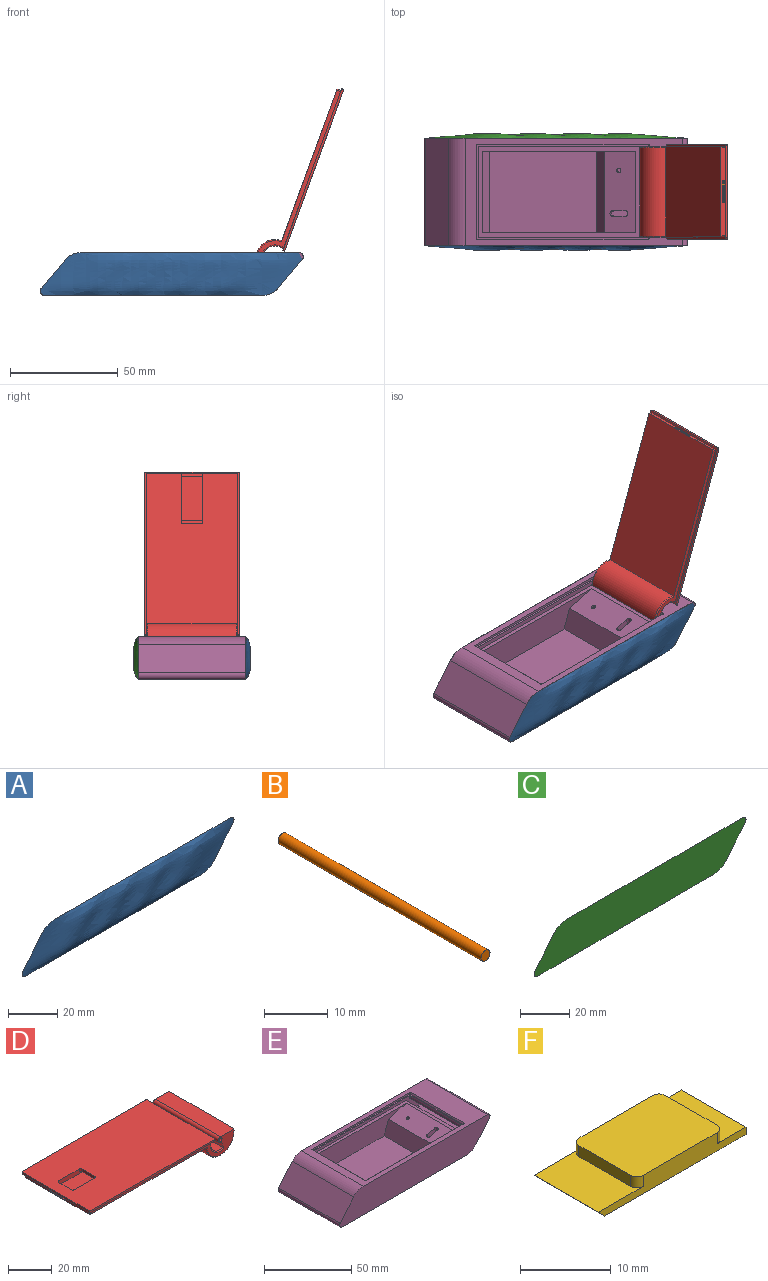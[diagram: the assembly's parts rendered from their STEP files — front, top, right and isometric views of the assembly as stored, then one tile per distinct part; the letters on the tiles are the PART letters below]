
ASSEMBLY  parts=6 mates=5
PART A: 2 faces, bbox 122.5x3.4x21.2 mm
  f0: plane 122.43x20.21mm, normal (0,1,0), area 2185.9mm2, adj f1
  f1: bspline ~122.31x20.97mm, area 2254.9mm2, adj f0
PART B: 3 faces, bbox 2x45x2 mm
  f0: cylinder r=1mm len=45mm, axis (0,1,0), area 282.7mm2, adj f1,f2
  f1: plane 2x2mm, normal (0,-1,0), area 3.1mm2, adj f0
  f2: plane 2x2mm, normal (0,1,0), area 3.1mm2, adj f0
PART C: 2 faces, bbox 122.5x3.4x21.2 mm
  f0: plane 122.43x20.21mm, normal (0,-1,0), area 2185.9mm2, adj f1
  f1: bspline ~122.31x20.97mm, area 2254.9mm2, adj f0
PART D: 38 faces, bbox 94.7x44x13.2 mm
  f0: plane 80.53x44mm, normal (0,0,1), area 3393.8mm2, adj f13,f14,f15,f16,f17,f18,f19,f20
  f1: plane 10x6mm, normal (0,0,-1), area 50.4mm2, adj f3,f30,f31,f35,f36,f37
  f2: cylinder r=6mm len=41mm, axis (0,1,0), area 555.9mm2, adj f8,f12,f22,f25
  f3: plane 41x2mm, normal (-1,0,0), area 72mm2, adj f1,f4,f12,f21,f24,f28,f30,f31
  f4: plane 75.5x42mm, normal (0,0,-1), area 3150mm2, adj f3,f5,f10,f11,f21,f23,f24,f26
  f5: cylinder r=9mm len=41mm, axis (0,1,0), area 1221mm2, adj f4,f6,f23,f26
  f6: plane 42x8.87mm, normal (0,0,1), area 372.6mm2, adj f5,f7,f10,f11,f23,f26
  f7: cylinder r=1.5mm len=42mm, axis (0,1,0), area 219.9mm2, adj f6,f8,f10,f11
  f8: plane 42x4.7mm, normal (-0.94,0,-0.34), area 189.1mm2, adj f2,f7,f10,f11,f22,f25
  f9: cylinder r=1mm len=42mm, axis (0,1,0), area 263.9mm2, adj f10,f11
  f10: plane 92x10.5mm, normal (0,-1,0), area 240.6mm2, adj f4,f6,f7,f8,f9,f12,f24,f25
  f11: plane 92x10.5mm, normal (0,1,0), area 240.6mm2, adj f4,f6,f7,f8,f9,f12,f21,f22
  f12: plane 80x44mm, normal (0,0,-1), area 229.6mm2, adj f2,f3,f10,f11,f13,f14,f15,f16
  f13: plane 43x1mm, normal (-1,0,0), area 43mm2, adj f0,f12,f17,f19
  f14: cylinder r=5.39mm len=43mm, axis (0,1,0), area 48.7mm2, adj f0,f12,f18,f20
  f15: plane 79.44x1mm, normal (0,-1,0), area 79.2mm2, adj f0,f12,f19,f20
  f16: plane 79.44x1mm, normal (0,1,0), area 79.2mm2, adj f0,f12,f17,f18
  f17: cylinder r=0.5mm len=1mm, axis (0,0,-1), area 0.8mm2, adj f0,f12,f13,f16
  f18: torus R=5.89mm, axis (0,-1,0), area 0.9mm2, adj f0,f12,f14,f16
  f19: cylinder r=0.5mm len=1mm, axis (0,0,1), area 0.8mm2, adj f0,f12,f13,f15
  f20: torus R=5.89mm, axis (0,-1,0), area 0.9mm2, adj f0,f12,f14,f15
  f21: cylinder r=0.5mm len=2mm, axis (0,0,-1), area 1.6mm2, adj f3,f4,f11,f12
  f22: torus R=6.5mm, axis (0,-1,0), area 10.9mm2, adj f2,f8,f11,f12
  f23: torus R=8.5mm, axis (0,-1,0), area 22.9mm2, adj f4,f5,f6,f11
  f24: cylinder r=0.5mm len=2mm, axis (0,0,1), area 1.6mm2, adj f3,f4,f10,f12
  f25: torus R=6.5mm, axis (0,-1,0), area 10.9mm2, adj f2,f8,f10,f12
  f26: torus R=8.5mm, axis (0,-1,0), area 22.9mm2, adj f4,f5,f6,f10
  f27: plane 10x6mm, normal (0,0,-1), area 50.4mm2, adj f29,f30,f31,f32,f33,f34
  f28: plane 25x10mm, normal (0,0,1), area 250mm2, adj f3,f29,f30,f31
  f29: plane 10x1mm, normal (-1,0,0), area 10mm2, adj f27,f28,f30,f31
  f30: plane 25x2.5mm, normal (0,1,0), area 44.5mm2, adj f0,f1,f3,f27,f28,f29,f32,f37
  f31: plane 25x2.5mm, normal (0,-1,0), area 44.5mm2, adj f0,f1,f3,f27,f28,f29,f34,f35
  f32: cylinder r=1mm len=1.5mm, axis (0,0,1), area 2.4mm2, adj f0,f27,f30,f33
  f33: plane 8x1.5mm, normal (-1,0,0), area 12mm2, adj f0,f27,f32,f34
  f34: cylinder r=1mm len=1.5mm, axis (0,0,1), area 2.4mm2, adj f0,f27,f31,f33
  f35: cylinder r=1mm len=1.5mm, axis (0,0,1), area 2.4mm2, adj f0,f1,f31,f36
  f36: plane 8x1.5mm, normal (1,0,0), area 12mm2, adj f0,f1,f35,f37
  f37: cylinder r=1mm len=1.5mm, axis (0,0,1), area 2.4mm2, adj f0,f1,f30,f36
PART E: 95 faces, bbox 122.2x50x20.5 mm
  f0: plane 38x14.46mm, normal (-0.27,0,0.96), area 545.9mm2, adj f1,f36,f37,f38,f43,f44,f45,f46
  f1: plane 75.5x42mm, normal (0,0,1), area 452mm2, adj f0,f17,f19,f20,f25,f27,f30,f33
  f2: plane 101.05x50mm, normal (0,0,1), area 1509.4mm2, adj f3,f9,f10,f11,f12,f14,f15,f16
  f3: cylinder r=10mm len=50mm, axis (0,1,0), area 436.3mm2, adj f2,f4,f10,f11
  f4: plane 50x13.14mm, normal (-0.77,0,0.64), area 857.8mm2, adj f3,f5,f10,f11
  f5: cylinder r=2mm len=50mm, axis (0,1,0), area 226.9mm2, adj f4,f6,f10,f11
  f6: plane 101.05x50mm, normal (0,0,-1), area 5052.4mm2, adj f5,f7,f10,f11
  f7: cylinder r=10mm len=50mm, axis (0,1,0), area 436.3mm2, adj f6,f8,f10,f11
  f8: plane 50x13.14mm, normal (0.77,0,-0.64), area 857.8mm2, adj f7,f9,f10,f11
  f9: cylinder r=2mm len=50mm, axis (0,1,0), area 226.9mm2, adj f2,f8,f10,f11
  f10: plane 122.2x20mm, normal (0,-1,0), area 2185.9mm2, adj f2,f3,f4,f5,f6,f7,f8,f9
  f11: plane 122.2x20mm, normal (0,1,0), area 2185.9mm2, adj f2,f3,f4,f5,f6,f7,f8,f9
  f12: plane 43x1mm, normal (1,0,0), area 43mm2, adj f2,f13,f21,f23
  f13: plane 80x44mm, normal (0,0,1), area 229.6mm2, adj f12,f14,f15,f16,f17,f18,f19,f20
  f14: cylinder r=5.39mm len=43mm, axis (0,1,0), area 48.7mm2, adj f2,f13,f22,f24
  f15: plane 79.44x1mm, normal (0,1,0), area 79.2mm2, adj f2,f13,f23,f24
  f16: plane 79.44x1mm, normal (0,-1,0), area 79.2mm2, adj f2,f13,f21,f22
  f17: plane 41x2mm, normal (1,0,0), area 72mm2, adj f1,f13,f25,f27,f59,f60,f61,f62
  f18: cylinder r=6mm len=41mm, axis (0,-1,0), area 83.6mm2, adj f13,f26,f28,f29
  f19: plane 92x10.5mm, normal (0,-1,0), area 279mm2, adj f1,f13,f27,f28,f29,f31,f32,f57
  f20: plane 92x10.5mm, normal (0,1,0), area 279mm2, adj f1,f13,f25,f26,f29,f31,f32,f56
  f21: cylinder r=0.5mm len=1mm, axis (0,0,1), area 0.8mm2, adj f2,f12,f13,f16
  f22: torus R=5.89mm, axis (0,-1,0), area 0.9mm2, adj f2,f13,f14,f16
  f23: cylinder r=0.5mm len=1mm, axis (0,0,-1), area 0.8mm2, adj f2,f12,f13,f15
  f24: torus R=5.89mm, axis (0,-1,0), area 0.9mm2, adj f2,f13,f14,f15
  f25: cylinder r=0.5mm len=2mm, axis (0,0,1), area 1.6mm2, adj f1,f13,f17,f20
  f26: torus R=6.5mm, axis (0,-1,0), area 1.6mm2, adj f13,f18,f20,f29
  f27: cylinder r=0.5mm len=2mm, axis (0,0,-1), area 1.6mm2, adj f1,f13,f17,f19
  f28: torus R=6.5mm, axis (0,-1,0), area 1.6mm2, adj f13,f18,f19,f29
  f29: plane 42x5mm, normal (0,0,-1), area 189.1mm2, adj f18,f19,f20,f26,f28,f32
  f30: cylinder r=9mm len=41mm, axis (0,1,0), area 1221mm2, adj f1,f31,f63,f64
  f31: plane 42x8.87mm, normal (0,0,-1), area 372.6mm2, adj f19,f20,f30,f32,f63,f64
  f32: cylinder r=1.5mm len=42mm, axis (0,1,0), area 99mm2, adj f19,f20,f29,f31
  f33: plane 38x4mm, normal (0.8,0,0.6), area 190mm2, adj f1,f34,f37,f38
  f34: plane 38x10mm, normal (1,0,0), area 380mm2, adj f33,f35,f37,f38
  f35: plane 50x38mm, normal (0,0,1), area 1900mm2, adj f34,f36,f37,f38
  f36: plane 38x10mm, normal (-0.94,0,0.33), area 403.1mm2, adj f0,f35,f37,f38
  f37: plane 71x14mm, normal (0,-1,0), area 766.8mm2, adj f0,f1,f33,f34,f35,f36
  f38: plane 71x14mm, normal (0,1,0), area 766.8mm2, adj f0,f1,f33,f34,f35,f36
  f39: plane 3x1.93mm, normal (-0.96,0,-0.27), area 6mm2, adj f40,f42,f47,f54
  f40: plane 3.42x2.73mm, normal (0,-1,0), area 6mm2, adj f39,f41,f47,f54
  f41: plane 3x1.93mm, normal (0.96,0,0.27), area 6mm2, adj f40,f42,f47,f54
  f42: plane 3.42x2.73mm, normal (0,1,0), area 6mm2, adj f39,f41,f47,f54
  f43: plane 6.58x4.49mm, normal (0,1,0), area 18mm2, adj f0,f44,f46,f47
  f44: cylinder r=1.3mm len=3.24mm, axis (-0.27,0,0.96), area 12.3mm2, adj f0,f43,f45,f47
  f45: plane 6.58x4.49mm, normal (0,-1,0), area 18mm2, adj f0,f44,f46,f47
  f46: cylinder r=1.3mm len=3.24mm, axis (-0.27,0,0.96), area 12.3mm2, adj f0,f43,f45,f47
  f47: plane 42x12.15mm, normal (0.27,0,-0.96), area 499.6mm2, adj f39,f40,f41,f42,f43,f44,f45,f46
  f48: plane 42x17.2mm, normal (0,0,1), area 722.3mm2, adj f49,f50,f51,f52
  f49: plane 42x9.89mm, normal (-0.96,0,-0.27), area 430.9mm2, adj f47,f48,f51,f52
  f50: plane 42x6.53mm, normal (0.94,0,-0.33), area 290.8mm2, adj f47,f48,f51,f52
  f51: plane 17.2x9.89mm, normal (0,1,0), area 120.8mm2, adj f47,f48,f49,f50
  f52: plane 17.2x9.89mm, normal (0,-1,0), area 120.8mm2, adj f47,f48,f49,f50
  f53: cylinder r=1mm len=2.19mm, axis (-0.27,0,0.96), area 6.3mm2, adj f0,f54
  f54: plane 3x2.89mm, normal (0.27,0,-0.96), area 5.9mm2, adj f39,f40,f41,f42,f53
  f55: plane 2x2mm, normal (0,1,0), area 3.1mm2, adj f56
  f56: cylinder r=1mm len=2mm, axis (0,1,0), area 9.4mm2, adj f20,f55
  f57: cylinder r=1mm len=2mm, axis (0,1,0), area 9.4mm2, adj f19,f58
  f58: plane 2x2mm, normal (0,-1,0), area 3.1mm2, adj f57
  f59: plane 10x1mm, normal (0,0,-1), area 10mm2, adj f17,f60,f61,f62
  f60: plane 10x1mm, normal (0.71,0,0.71), area 14.1mm2, adj f17,f59,f61,f62
  f61: plane 1x1mm, normal (0,-1,0), area 0.5mm2, adj f17,f59,f60
  f62: plane 1x1mm, normal (0,1,0), area 0.5mm2, adj f17,f59,f60
  f63: torus R=8.5mm, axis (0,-1,0), area 22.9mm2, adj f1,f19,f30,f31
  f64: torus R=8.5mm, axis (0,-1,0), area 22.9mm2, adj f1,f20,f30,f31
  f65: plane 42x9mm, normal (-1,0,0), area 378mm2, adj f66,f68,f69,f70
  f66: plane 42x14.62mm, normal (0,0,-1), area 614.1mm2, adj f65,f67,f69,f70
  f67: plane 42x9mm, normal (0.77,0,-0.64), area 493.4mm2, adj f66,f68,f69,f70
  f68: plane 42x22.17mm, normal (0,0,1), area 931.2mm2, adj f65,f67,f69,f70
  f69: plane 22.17x9mm, normal (0,1,0), area 165.6mm2, adj f65,f66,f67,f68
  f70: plane 22.17x9mm, normal (0,-1,0), area 165.6mm2, adj f65,f66,f67,f68
  f71: plane 42x1mm, normal (-1,0,0), area 42mm2, adj f72,f74,f75,f76
  f72: plane 50x42mm, normal (0,0,-1), area 2100mm2, adj f71,f73,f75,f76
  f73: plane 42x1mm, normal (1,0,0), area 42mm2, adj f72,f74,f75,f76
  f74: plane 50x42mm, normal (0,0,1), area 2100mm2, adj f71,f73,f75,f76
  f75: plane 50x1mm, normal (0,1,0), area 50mm2, adj f71,f72,f73,f74
  f76: plane 50x1mm, normal (0,-1,0), area 50mm2, adj f71,f72,f73,f74
  f77: plane 40x2mm, normal (-1,0,0), area 80mm2, adj f78,f80,f81,f82
  f78: plane 40x5mm, normal (0,0,-1), area 200mm2, adj f77,f79,f81,f82
  f79: plane 40x2mm, normal (1,0,0), area 80mm2, adj f78,f80,f81,f82
  f80: plane 40x5mm, normal (0,0,1), area 200mm2, adj f77,f79,f81,f82
  f81: plane 5x2mm, normal (0,-1,0), area 10mm2, adj f77,f78,f79,f80
  f82: plane 5x2mm, normal (0,1,0), area 10mm2, adj f77,f78,f79,f80
  f83: plane 40x2mm, normal (1,0,0), area 80mm2, adj f84,f86,f87,f88
  f84: plane 40x5mm, normal (0,0,1), area 200mm2, adj f83,f85,f87,f88
  f85: plane 40x2mm, normal (-1,0,0), area 80mm2, adj f84,f86,f87,f88
  f86: plane 40x5mm, normal (0,0,-1), area 200mm2, adj f83,f85,f87,f88
  f87: plane 5x2mm, normal (0,-1,0), area 10mm2, adj f83,f84,f85,f86
  f88: plane 5x2mm, normal (0,1,0), area 10mm2, adj f83,f84,f85,f86
  f89: plane 40x2mm, normal (-1,0,0), area 80mm2, adj f90,f92,f93,f94
  f90: plane 40x5mm, normal (0,0,-1), area 200mm2, adj f89,f91,f93,f94
  f91: plane 40x2mm, normal (1,0,0), area 80mm2, adj f90,f92,f93,f94
  f92: plane 40x5mm, normal (0,0,1), area 200mm2, adj f89,f91,f93,f94
  f93: plane 5x2mm, normal (0,-1,0), area 10mm2, adj f89,f90,f91,f92
  f94: plane 5x2mm, normal (0,1,0), area 10mm2, adj f89,f90,f91,f92
PART F: 14 faces, bbox 23x10x2.5 mm
  f0: plane 10x4.5mm, normal (0,0,1), area 35.4mm2, adj f4,f5,f6,f7,f8,f9
  f1: plane 10x7mm, normal (0,0,1), area 60.4mm2, adj f2,f5,f6,f10,f11,f12
  f2: plane 10x1mm, normal (-0.71,0,-0.71), area 14.1mm2, adj f1,f3,f5,f6
  f3: plane 22x10mm, normal (0,0,-1), area 220mm2, adj f2,f4,f5,f6
  f4: plane 10x1mm, normal (1,0,0), area 10mm2, adj f0,f3,f5,f6
  f5: plane 23x2.5mm, normal (0,-1,0), area 39.8mm2, adj f0,f1,f2,f3,f4,f7,f12,f13
  f6: plane 23x2.5mm, normal (0,1,0), area 39.8mm2, adj f0,f1,f2,f3,f4,f9,f10,f13
  f7: cylinder r=1mm len=1.5mm, axis (0,0,1), area 2.4mm2, adj f0,f5,f8,f13
  f8: plane 8x1.5mm, normal (1,0,0), area 12mm2, adj f0,f7,f9,f13
  f9: cylinder r=1mm len=1.5mm, axis (0,0,1), area 2.4mm2, adj f0,f6,f8,f13
  f10: cylinder r=1mm len=1.5mm, axis (0,0,1), area 2.4mm2, adj f1,f6,f11,f13
  f11: plane 8x1.5mm, normal (-1,0,0), area 12mm2, adj f1,f10,f12,f13
  f12: cylinder r=1mm len=1.5mm, axis (0,0,1), area 2.4mm2, adj f1,f5,f11,f13
  f13: plane 13.5x10mm, normal (0,0,1), area 134.1mm2, adj f5,f6,f7,f8,f9,f10,f11,f12
PLACE A t=(-76.26,0,-10)mm
PLACE B rot(axis=(-0.17,0,-0.98),180deg) t=(172.27,0,-53.82)mm
PLACE C t=(-76.26,0,-10)mm
PLACE D rot(axis=(0,1,0),110deg) t=(76.71,0,151.11)mm
PLACE E t=(-76.26,0,-10)mm
PLACE F rot(axis=(0,1,0),110deg) t=(76.2,0,149.7)mm
MATE fastened C.f0 <-> E.f11  axis (0,-1,0) through (8.58,25,10)mm
MATE slider B.f0 <-> D.f2  axis (0,-1,0) through (56.63,0,17)mm
MATE pin_slot D.f0 <-> F.f13  axis (0.94,0,-0.34) through (86.47,0,90.21)mm
MATE cylindrical D.f2 <-> E.f14  axis (0,1,0) through (56.63,0,17)mm
MATE fastened A.f0 <-> E.f10  axis (0,1,0) through (8.58,-25,10)mm
